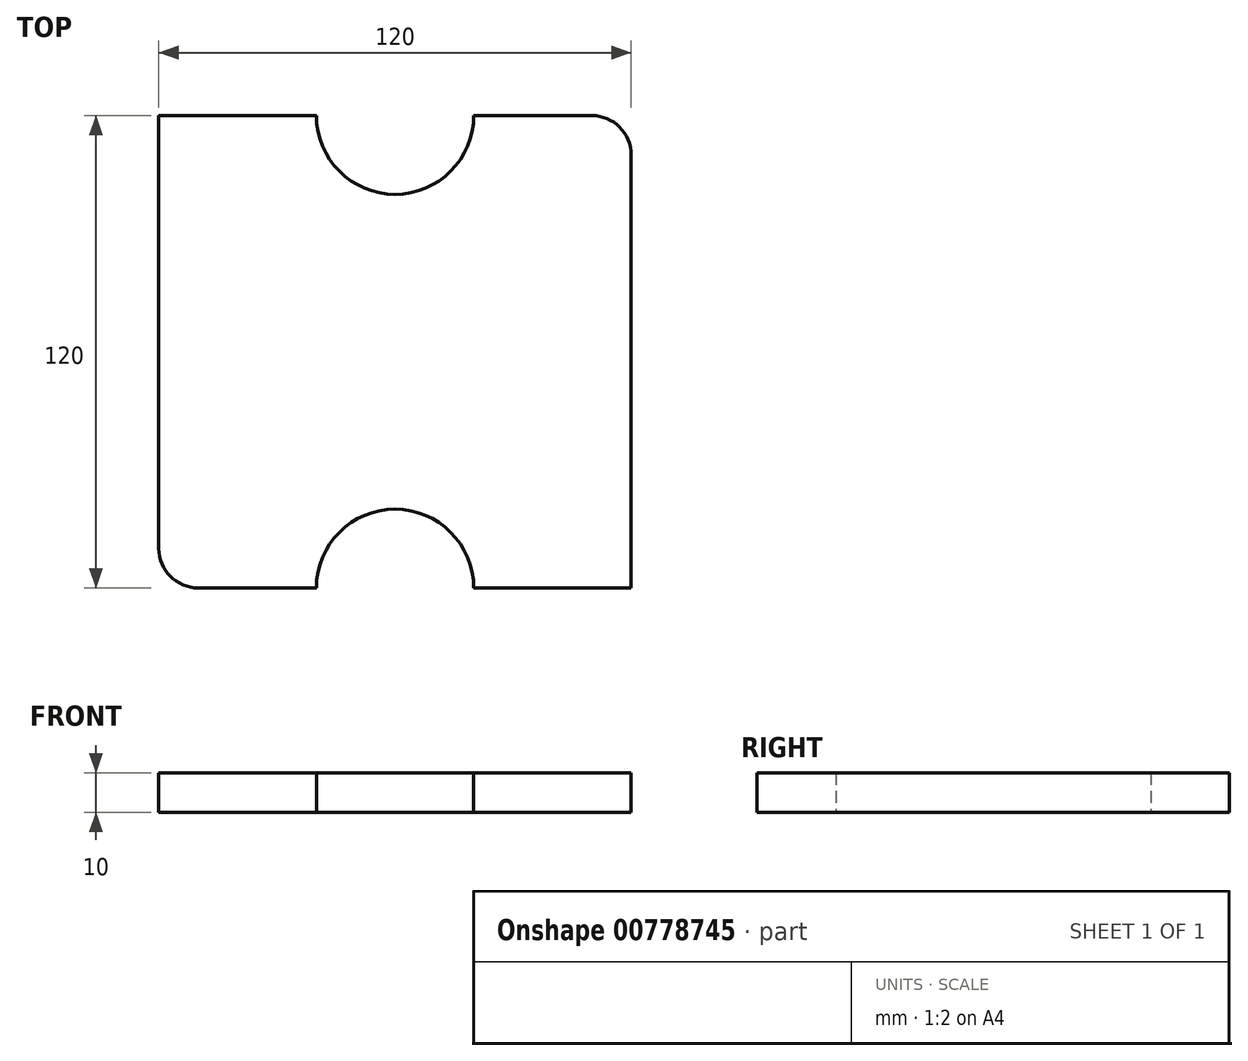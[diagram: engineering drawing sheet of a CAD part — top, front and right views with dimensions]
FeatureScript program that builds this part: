
annotation { "Feature Type Name" : "Feature", "Feature Type Description" : "" }
export const myFeature = defineFeature(function(context is Context, id is Id, definition is map)
    precondition{}
    {
        {
            var Q0;
            Q0=qCreatedBy(makeId("Top.planeOp"),FACE);
            var sketch = newSketch(context, id + "F0", { "sketchPlane" : qUnion([Q0])});
            skLineSegment(sketch, "E0.bottom", {"start": v(10, 0) * mm, "end": v(40, 0) * mm});
            skLineSegment(sketch, "E0.top", {"start": v(0, 120) * mm, "end": v(40, 120) * mm});
            skLineSegment(sketch, "E0.left", {"start": v(0, 10) * mm, "end": v(0, 120) * mm});
            skLineSegment(sketch, "E0.right", {"start": v(120, 0) * mm, "end": v(120, 120) * mm});
            skPoint(sketch, "E1.visualSharp", {"position": v(0, 0) * mm});
            skArc(sketch, "E1.filletArc", {"start": v(0, 10) * mm, "mid": v(2.93, 2.93) * mm, "end": v(10, 0) * mm});
            skArc(sketch, "E2", {"start": v(80, 0) * mm, "mid": v(60, 20) * mm, "end": v(40, 0) * mm});
            skLineSegment(sketch, "E3.trimOffspring", {"start": v(80, 0) * mm, "end": v(120, 0) * mm});
            skArc(sketch, "E4", {"start": v(40, 120) * mm, "mid": v(60, 100) * mm, "end": v(80, 120) * mm});
            skLineSegment(sketch, "E5.trimOffspring", {"start": v(80, 120) * mm, "end": v(120, 120) * mm});
            skSolve(sketch);
        }
        {
            var Q0;
            Q0=makeQuery(id+"F0.imprint","IMPRINT",FACE,{"disambiguationData":[TD([[makeQuery(id+"F0.imprint","IMPRINT",EDGE,{"derivedFrom":sQuery(id+"F0.wireOp",EDGE,"E0.bottom")}),1.0]])]});
            extrude(context, id + "F1", {"entities" : qUnion([Q0]), "depth" : 10 * mm, "offsetDistance" : 25 * mm});
        }
        {
            var Q0;
            Q0=makeQuery(id+"F1.opExtrude","SWEPT_EDGE",EDGE,{"disambiguationData":[OSD([sQuery(id+"F0.wireOp",EDGE,"E0.right"),sQuery(id+"F0.wireOp",EDGE,"E5.trimOffspring")])]});
            fillet(context, id + "F2", {"entities" : qUnion([Q0]), "tangentPropagation" : true, "radius" : 10 * mm, "defaultsChanged" : false, "vertexSettings" : [], "allowEdgeOverflow" : false});
        }
    });
